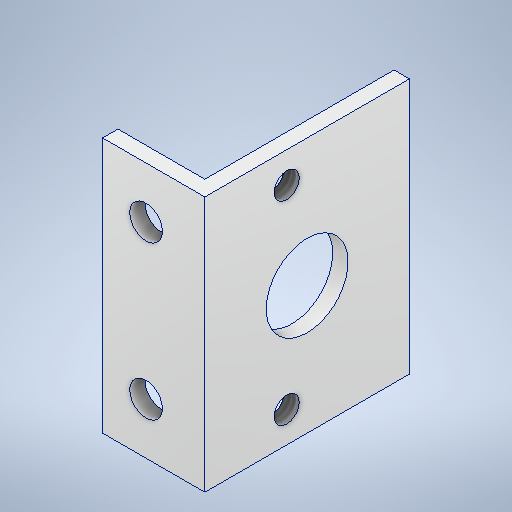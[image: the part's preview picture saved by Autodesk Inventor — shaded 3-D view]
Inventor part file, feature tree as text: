
AUTODESK INVENTOR PART (.ipt)
format: ipt  version: 2025 (Build 290162000, 162)  size: 283,648 bytes
history: native  units: mm
features: sketch x4, hole x3, projected_geometry x3, other x1, extrude x1
ambient origin geometry x8: Origin, YZ Plane, XZ Plane, XY Plane, X Axis, Y Axis, Z Axis, Center Point
bodies: Body1 (feature_tree)
feature tree (12):
  other  "Těleso1"
  extrude  "Vysunutí1"  Depth=20.0mm
  hole  "Díra1"  [1 undecoded]
  hole  "Díra5"  [1 undecoded]
  hole  "Díra6"  [1 undecoded]
  sketch  "Náčrt1"
  sketch  "Náčrt2"
  projected_geometry  "Promítnutá smyčka1"
  sketch  "Náčrt7"
  projected_geometry  "Promítnutá smyčka5"
  sketch  "Náčrt8"
  projected_geometry  "Promítnutá smyčka6"
note: 3 required parameter values undecoded (feature->parameter linkage not recoverable at this tier; creation-order binding heuristic only, values carry confidence <= 0.55)
